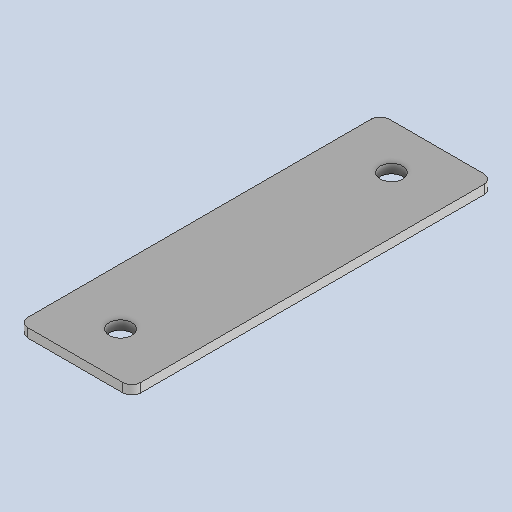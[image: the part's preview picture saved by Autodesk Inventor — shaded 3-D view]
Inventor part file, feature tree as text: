
AUTODESK INVENTOR PART (.ipt)
format: ipt  version: 2025 (Build 290162010, 162A)  size: 138,240 bytes
history: native  units: mm
features: sketch x2, other x2, sheet_metal_op x1, extrude x1, fillet x1, projected_geometry x1
ambient origin geometry x8: Origin, YZ Plane, XZ Plane, XY Plane, X Axis, Y Axis, Z Axis, Center Point
bodies: Solid1 (feature_tree)
feature tree (8):
  sheet_metal_op  "Face1"
  extrude  "Extrusion3"  Depth=80.0mm
  fillet  "Fillet2"  Radius=2.0mm
  sketch  "Sketch1"  dims[d0=25.0mm d1=80.0mm d2=2.0mm]
  other  "Plate1"
  sketch  "Sketch8"  dims[d34=5.0mm d35=10.0mm d36=0.0mm d37=0.0mm d38=2.0mm]
  projected_geometry  "Projected Loop3"
  other  "Definition1"
